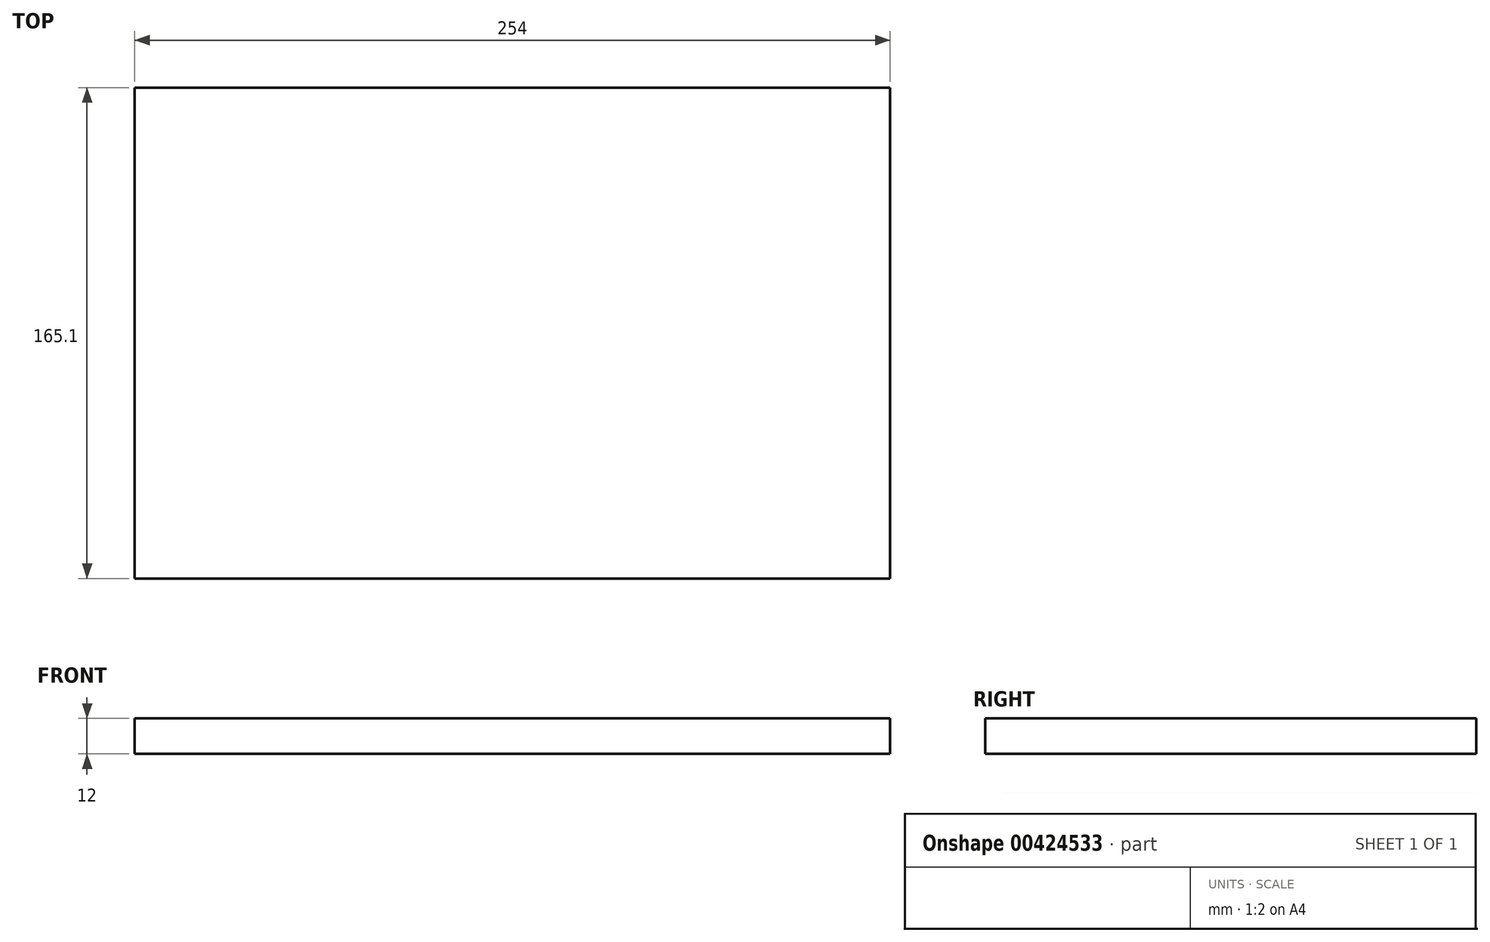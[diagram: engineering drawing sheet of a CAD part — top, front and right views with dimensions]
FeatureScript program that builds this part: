
annotation { "Feature Type Name" : "Feature", "Feature Type Description" : "" }
export const myFeature = defineFeature(function(context is Context, id is Id, definition is map)
    precondition{}
    {
        {
            var Q0;
            Q0=qCreatedBy(makeId("Top.planeOp"),FACE);
            var sketch = newSketch(context, id + "F0", { "sketchPlane" : qUnion([Q0])});
            skLineSegment(sketch, "E0.bottom", {"start": v(-108.07, 79.12) * mm, "end": v(145.93, 79.12) * mm});
            skLineSegment(sketch, "E0.top", {"start": v(-108.07, -85.98) * mm, "end": v(145.93, -85.98) * mm});
            skLineSegment(sketch, "E0.left", {"start": v(-108.07, 79.12) * mm, "end": v(-108.07, -85.98) * mm});
            skLineSegment(sketch, "E0.right", {"start": v(145.93, 79.12) * mm, "end": v(145.93, -85.98) * mm});
            skSolve(sketch);
        }
        {
            var Q0;
            Q0=makeQuery(id+"F0.imprint","IMPRINT",FACE,{"disambiguationData":[TD([[makeQuery(id+"F0.imprint","IMPRINT",EDGE,{"derivedFrom":sQuery(id+"F0.wireOp",EDGE,"E0.bottom")}),-1.0]])]});
            extrude(context, id + "F1", {"entities" : qUnion([Q0]), "depth" : 12 * mm});
        }
    });
